# Revit family: Daylight_Sensor-Lutron-Radio_Powr_Savr-LRFDCRBWH--
name_source: partatom
category: Lighting Devices
revit_build: Autodesk Revit 2015 (Build: 20160512_0715(x64)
units: mm (PartAtom-declared; Revit-internal decimal feet)

## types (1)
- ERROR_LOAD Type Catalog
    Arrow Light Horizontal Offset = 0.074 "
    Arrow Light Tip Depth Offset = 0.015 "
    Arrow Vertical Offset = 0.057 "
    Arrow Void Depth = 0.25 "
    Arrow Void Height = 0.109 "
    Arrow Void Horizontal Offset = 0.128 "
    Arrow Void Tip Depth Offset = 0.143 "
    Assembly Code = D5030800
    Bottom Cover Radius = 2.676 "
    Button Height = 0.044 "
    Button Vertical Offset = 0.009 "
    Center Button Depth Offset = 0.311 "
    Cover Angle = 165.00°
    Cover Height = 0.18 "
    Current = 0 A
    Default Elevation = 0 "
    Description = Wireless Daylight Sensor
    ENGworks URL = http://www.ENGworks.com
    Electrical Potential = 3 V
    Frequency and Channel Codes = 431.0 - 437.0 MHz (U.S.A.; Canada; Mexico; Brazil)
    Label = DS
    Light Range = 150 fc
    Manufacturer = Lutron Electronics
    Maximum Operating Temperature = 104 °F
    Minimum Operating Temperature = 32 °F
    Model = LRF2-DCRB-WH
    Overall Depth = 1.6 "
    Overall Height = 0.7 "
    Overall Width = 1.6 "
    Product Page URL = http://www.lutron.com
    Range = 360 "
    Range End Angle = 172.50°
    Range Start Angle = 7.50°
    Sensor Bottom Body Height = 0.271 "
    Sensor Cover Angle = 195.00°
    Sensor Material = Plastic - Lutron - White
    Sensor Radius = 0.8 "
    Sensor Top Body Height = 0.264 "
    Series = Radio Powr Savr
    Side Buttons Depth Offset = 0.167 "
    Side Buttons Horizontal Offset = 0.4 "
    Standards = FCC certified; IC certified; COFETEL; ANATEL; ASEP; CRC; SUBTEL; SUPERTEL; SUTEL; cULus Listed; Meets CA (U.S.A.) Energy Commission Title 24 requirements.
    Thomas Enterprise Solutions URL = http://www.thomasenterprisesolutions.com
    URL = http://www.lutron.com
    Version = 1

## geometry (parser evidence)
native form markers: Blend x18, Sweep x2
no freeform markers — native parametric forms only
